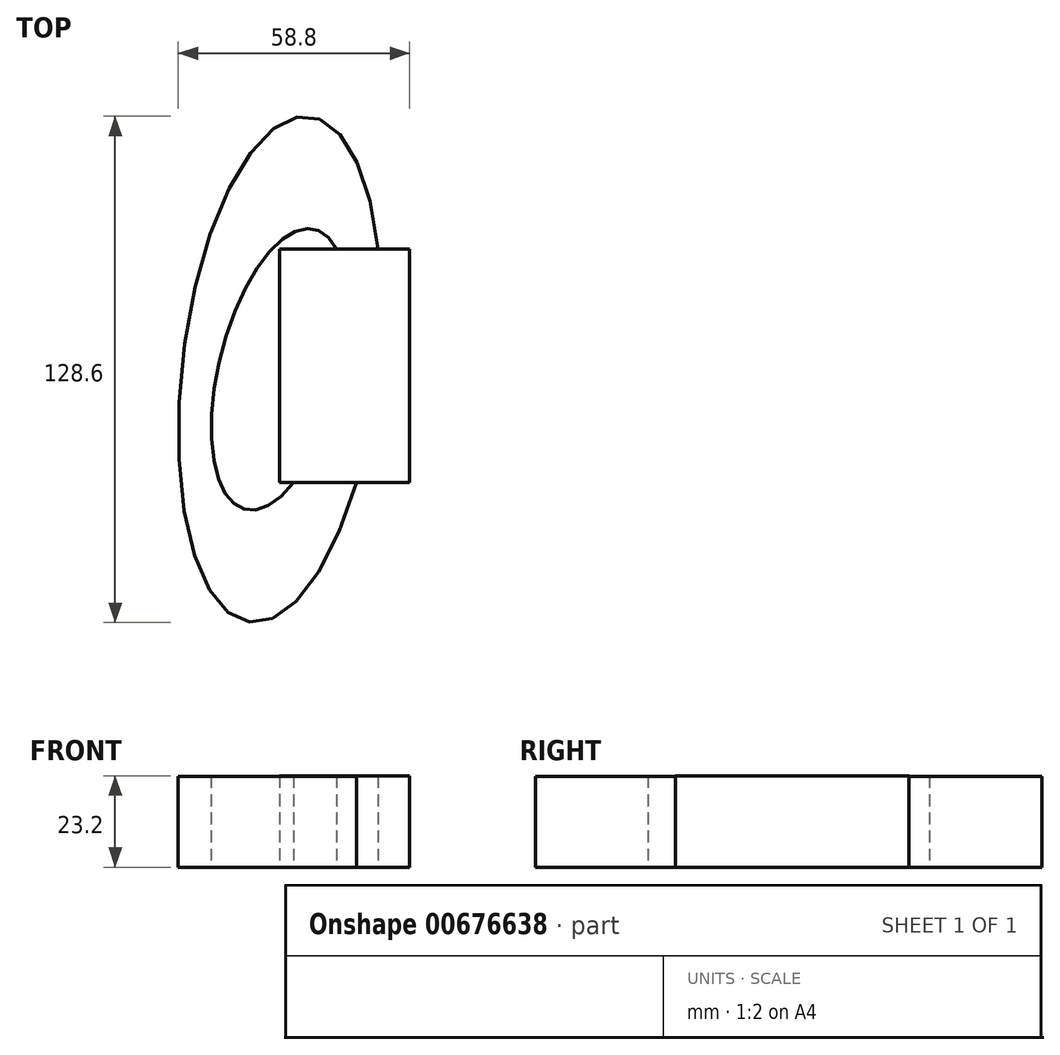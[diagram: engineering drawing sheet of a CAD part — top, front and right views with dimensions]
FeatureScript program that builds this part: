
annotation { "Feature Type Name" : "Feature", "Feature Type Description" : "" }
export const myFeature = defineFeature(function(context is Context, id is Id, definition is map)
    precondition{}
    {
        {
            var Q0;
            Q0=qCreatedBy(makeId("Top.planeOp"),FACE);
            var sketch = newSketch(context, id + "F0", { "sketchPlane" : qUnion([Q0])});
            skEllipse(sketch, "E0", {"center": v(0, 0) * mm, "majorRadius": 64.68 * mm, "minorRadius": 24.82 * mm, "majorAxis": v(-0.12, -1)});
            skSolve(sketch);
        }
        {
            var Q0;
            Q0 = qSketchRegion(id + "F0", true);
            extrude(context, id + "F1", {"entities" : qUnion([Q0]), "depth" : 23.1 * mm, "offsetDistance" : 25.4 * mm});
        }
        {
            var Q0;
            Q0=qCreatedBy(makeId("Top.planeOp"),FACE);
            var sketch = newSketch(context, id + "F2", { "sketchPlane" : qUnion([Q0])});
            skEllipse(sketch, "E1", {"center": v(0, 0) * mm, "majorRadius": 36.67 * mm, "minorRadius": 15.43 * mm, "majorAxis": v(-0.24, -0.97)});
            skSolve(sketch);
        }
        {
            var Q0;
            Q0 = qSketchRegion(id + "F2", true);
            extrude(context, id + "F3", {"entities" : qUnion([Q0]), "operationType" : NewBodyOperationType.REMOVE, "depth" : 60.45 * mm, "offsetDistance" : 25.4 * mm});
        }
        {
            var Q0;
            Q0=qCreatedBy(makeId("Right.planeOp"),FACE);
            var sketch = newSketch(context, id + "F4", { "sketchPlane" : qUnion([Q0])});
            skLineSegment(sketch, "E2.bottom", {"start": v(-28.77, 23.2) * mm, "end": v(30.54, 23.2) * mm});
            skLineSegment(sketch, "E2.top", {"start": v(-28.77, 0) * mm, "end": v(30.54, 0) * mm});
            skLineSegment(sketch, "E2.left", {"start": v(-28.77, 23.2) * mm, "end": v(-28.77, 0) * mm});
            skLineSegment(sketch, "E2.right", {"start": v(30.54, 23.2) * mm, "end": v(30.54, 0) * mm});
            skSolve(sketch);
        }
        {
            var Q0;
            Q0 = qSketchRegion(id + "F4", true);
            extrude(context, id + "F5", {"entities" : qUnion([Q0]), "operationType" : NewBodyOperationType.ADD, "depth" : 33.02 * mm, "offsetDistance" : 25.4 * mm});
        }
    });
